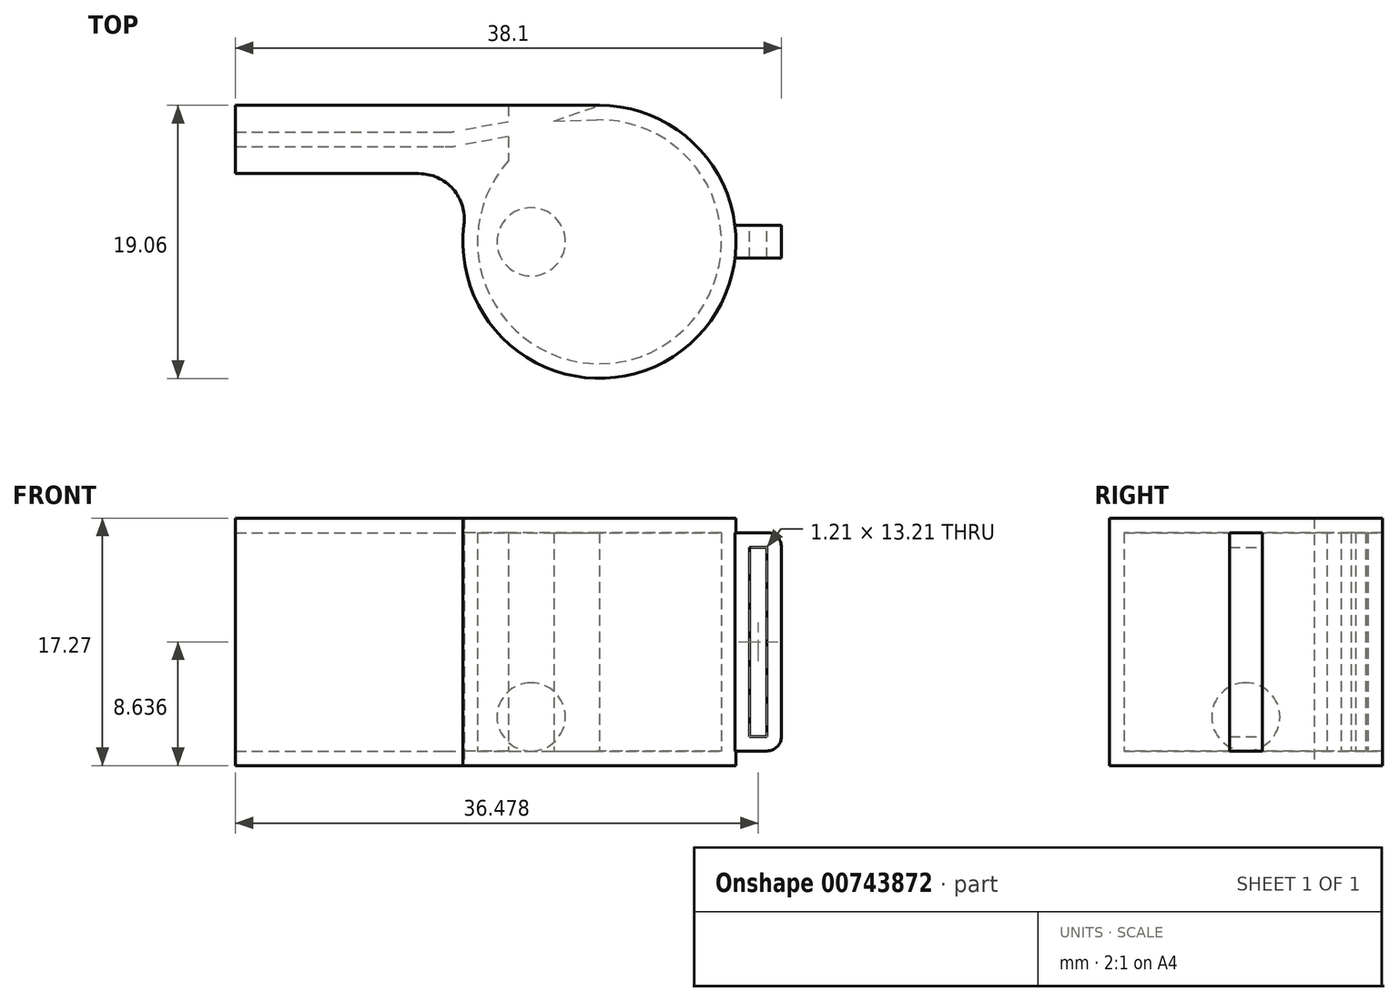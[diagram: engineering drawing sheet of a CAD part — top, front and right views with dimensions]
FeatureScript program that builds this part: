
annotation { "Feature Type Name" : "Feature", "Feature Type Description" : "" }
export const myFeature = defineFeature(function(context is Context, id is Id, definition is map)
    precondition{}
    {
        {
            var Q0;
            Q0=qCreatedBy(makeId("Top.planeOp"),FACE);
            var sketch = newSketch(context, id + "F0", { "sketchPlane" : qUnion([Q0])});
            skArc(sketch, "E0", {"start": v(-9.45, 1.2) * mm, "mid": v(6.3, -7.14) * mm, "end": v(0, 9.53) * mm});
            skLineSegment(sketch, "E1", {"start": v(-6.35, 9.53) * mm, "end": v(-25.4, 9.53) * mm});
            skLineSegment(sketch, "E2", {"start": v(-25.4, 9.52) * mm, "end": v(-25.4, 4.76) * mm});
            skLineSegment(sketch, "E3", {"start": v(-25.4, 4.76) * mm, "end": v(-12.6, 4.76) * mm});
            skPoint(sketch, "E4.visualSharp", {"position": v(-8.25, 4.76) * mm});
            skArc(sketch, "E4.filletArc", {"start": v(-9.45, 1.2) * mm, "mid": v(-10.22, 3.69) * mm, "end": v(-12.6, 4.76) * mm});
            skArc(sketch, "E5.0", {"start": v(-8.44, 1.06) * mm, "mid": v(5.7, -6.32) * mm, "end": v(-0.2, 8.5) * mm, "construction": true});
            skLineSegment(sketch, "E6", {"start": v(-3.18, 7.9) * mm, "end": v(-3.18, 8.98) * mm});
            skPoint(sketch, "E7.orphan", {"position": v(0, 9.53) * mm});
            skLineSegment(sketch, "E8", {"start": v(-3.18, 8.44) * mm, "end": v(0, 9.53) * mm, "construction": true});
            skLineSegment(sketch, "E9", {"start": v(-3.18, 8.44) * mm, "end": v(0, 8.51) * mm, "construction": true});
            skArc(sketch, "E10.trimOffspring", {"start": v(-3.18, 7.9) * mm, "mid": v(-3.56, 7.73) * mm, "end": v(-3.93, 7.55) * mm, "construction": true});
            skArc(sketch, "E11.trimOffspring", {"start": v(-3.17, 8.98) * mm, "mid": v(-3.74, 8.76) * mm, "end": v(-4.28, 8.5) * mm, "construction": true});
            skLineSegment(sketch, "E12", {"start": v(-6.35, 18.63) * mm, "end": v(-6.35, 7.34) * mm});
            skLineSegment(sketch, "E13", {"start": v(0, 9.53) * mm, "end": v(0, 8.51) * mm, "construction": true});
            skLineSegment(sketch, "E14", {"start": v(0, 9.02) * mm, "end": v(-17.36, 5.84) * mm, "construction": true});
            skLineSegment(sketch, "E15", {"start": v(-25.4, 7.14) * mm, "end": v(-7.63, 7.14) * mm, "construction": true});
            skLineSegment(sketch, "E16.0", {"start": v(-0.1, 9.52) * mm, "end": v(-9.73, 7.76) * mm, "construction": true});
            skLineSegment(sketch, "E17.0", {"start": v(0.1, 8.52) * mm, "end": v(-9.63, 6.74) * mm, "construction": true});
            skLineSegment(sketch, "E18.0", {"start": v(-25.4, 6.64) * mm, "end": v(-10.78, 6.64) * mm});
            skLineSegment(sketch, "E19.0", {"start": v(-25.4, 7.65) * mm, "end": v(-10.87, 7.65) * mm});
            skPoint(sketch, "E20.visualSharp", {"position": v(-10.3, 7.65) * mm});
            skArc(sketch, "E20.filletArc", {"start": v(-10.87, 7.65) * mm, "mid": v(-10.3, 7.68) * mm, "end": v(-9.73, 7.76) * mm});
            skPoint(sketch, "E21.visualSharp", {"position": v(-10.2, 6.64) * mm});
            skArc(sketch, "E21.filletArc", {"start": v(-10.78, 6.64) * mm, "mid": v(-10.2, 6.66) * mm, "end": v(-9.63, 6.74) * mm});
            skLineSegment(sketch, "E22", {"start": v(-6.35, 9.53) * mm, "end": v(0, 9.53) * mm});
            skSolve(sketch);
        }
        {
            var Q0;
            Q0=makeQuery(id+"F0.imprint","IMPRINT",FACE,{"disambiguationData":[TD([[makeQuery(id+"F0.imprint","IMPRINT",EDGE,{"derivedFrom":sQuery(id+"F0.wireOp",EDGE,"E0")}),1.0]])]});
            extrude(context, id + "F1", {"entities" : qUnion([Q0]), "depth" : 1.02 * mm, "offsetDistance" : 25.4 * mm});
        }
        {
            var Q0;
            Q0=makeQuery(id+"F1.opExtrude","CAP_FACE",FACE,{"disambiguationData":[OSD([sQuery(id+"F0.wireOp",EDGE,"E0"),sQuery(id+"F0.wireOp",EDGE,"E1"),sQuery(id+"F0.wireOp",EDGE,"E2"),sQuery(id+"F0.wireOp",EDGE,"E3"),sQuery(id+"F0.wireOp",EDGE,"E4.filletArc"),sQuery(id+"F0.wireOp",EDGE,"E22")])],"isStart":false});
            var sketch = newSketch(context, id + "F2", { "sketchPlane" : qUnion([Q0]), "disableImprinting" : false});
            skLineSegment(sketch, "E23.0", {"start": v(-25.4, 7.65) * mm, "end": v(-10.87, 7.65) * mm});
            skLineSegment(sketch, "E24.0", {"start": v(-25.4, 6.64) * mm, "end": v(-10.78, 6.64) * mm});
            skArc(sketch, "E25.0", {"start": v(-10.87, 7.65) * mm, "mid": v(-10.3, 7.68) * mm, "end": v(-9.73, 7.76) * mm});
            skArc(sketch, "E26.0", {"start": v(-10.78, 6.64) * mm, "mid": v(-10.2, 6.66) * mm, "end": v(-9.63, 6.74) * mm});
            skLineSegment(sketch, "E27.0", {"start": v(0.1, 8.52) * mm, "end": v(0.04, 8.5) * mm});
            skLineSegment(sketch, "E28.0", {"start": v(-6.35, 8.37) * mm, "end": v(-9.73, 7.76) * mm});
            skLineSegment(sketch, "E29.0", {"start": v(-3.18, 8.44) * mm, "end": v(0, 8.51) * mm});
            skLineSegment(sketch, "E30.0", {"start": v(-3.18, 8.44) * mm, "end": v(0, 9.53) * mm});
            skArc(sketch, "E31.0", {"start": v(-6.35, 5.66) * mm, "mid": v(3.57, -7.72) * mm, "end": v(-0.2, 8.5) * mm});
            skPoint(sketch, "E32.orphan", {"position": v(-8.44, 1.06) * mm});
            skLineSegment(sketch, "E33.0", {"start": v(-6.35, 9.53) * mm, "end": v(-6.35, 8.37) * mm});
            skPoint(sketch, "E34.orphan", {"position": v(-6.35, 7.34) * mm});
            skLineSegment(sketch, "E35.trimOffspring", {"start": v(-6.35, 7.34) * mm, "end": v(-6.35, 5.66) * mm});
            skLineSegment(sketch, "E36.0", {"start": v(-6.35, 9.53) * mm, "end": v(0, 9.53) * mm, "construction": true});
            skPoint(sketch, "E37.orphan", {"position": v(-6.35, 18.63) * mm});
            skLineSegment(sketch, "E38.0", {"start": v(-6.35, 9.53) * mm, "end": v(-25.4, 9.53) * mm});
            skLineSegment(sketch, "E39.0", {"start": v(-25.4, 9.52) * mm, "end": v(-25.4, 7.65) * mm});
            skLineSegment(sketch, "E40.0", {"start": v(-25.4, 4.76) * mm, "end": v(-12.6, 4.76) * mm});
            skArc(sketch, "E41.0", {"start": v(-9.45, 1.2) * mm, "mid": v(-10.22, 3.69) * mm, "end": v(-12.6, 4.76) * mm});
            skArc(sketch, "E42.0", {"start": v(-9.45, 1.2) * mm, "mid": v(-1.17, -9.45) * mm, "end": v(9.46, -1.14) * mm});
            skLineSegment(sketch, "E43.trimOffspring", {"start": v(-6.35, 7.34) * mm, "end": v(-9.63, 6.74) * mm});
            skPoint(sketch, "E44.orphan", {"position": v(-0.1, 9.52) * mm});
            skLineSegment(sketch, "E45.trimOffspring", {"start": v(-25.4, 6.64) * mm, "end": v(-25.4, 4.76) * mm});
            skLineSegment(sketch, "E46", {"start": v(0, 0) * mm, "end": v(13.97, 0) * mm, "construction": true});
            skLineSegment(sketch, "E47.0", {"start": v(0, -1.14) * mm, "end": v(8.43, -1.14) * mm, "construction": true});
            skLineSegment(sketch, "E48.0", {"start": v(0, 1.14) * mm, "end": v(8.43, 1.14) * mm, "construction": true});
            skLineSegment(sketch, "E49", {"start": v(12.7, 1.14) * mm, "end": v(12.7, -1.14) * mm});
            skLineSegment(sketch, "E50.trimOffspring", {"start": v(9.46, -1.14) * mm, "end": v(12.7, -1.14) * mm});
            skLineSegment(sketch, "E51.trimOffspring", {"start": v(9.46, 1.14) * mm, "end": v(12.7, 1.14) * mm});
            skArc(sketch, "E52.trimOffspring", {"start": v(9.46, 1.14) * mm, "mid": v(6.32, 7.13) * mm, "end": v(0, 9.52) * mm});
            skSolve(sketch);
        }
        {
            var Q0;
            Q0=makeQuery(id+"F2.imprint","IMPRINT",FACE,{"disambiguationData":[TD([[makeQuery(id+"F2.imprint","IMPRINT",EDGE,{"derivedFrom":sQuery(id+"F2.wireOp",EDGE,"E24.0")}),-1.0]])]});
            var Q1;
            Q1=makeQuery(id+"F2.imprint","IMPRINT",FACE,{"disambiguationData":[TD([[makeQuery(id+"F2.imprint","IMPRINT",EDGE,{"derivedFrom":sQuery(id+"F2.wireOp",EDGE,"E23.0")}),1.0]])]});
            var Q2;
            Q2=makeQuery(id+"F2.imprint","IMPRINT",FACE,{"disambiguationData":[TD([[makeQuery(id+"F2.imprint","IMPRINT",EDGE,{"derivedFrom":sQuery(id+"F2.wireOp",EDGE,"E49")}),-1.0]])]});
            extrude(context, id + "F3", {"entities" : qUnion([Q0, Q1, Q2]), "operationType" : NewBodyOperationType.ADD, "depth" : 15.24 * mm, "offsetDistance" : 25.4 * mm});
        }
        {
            var Q0;
            Q0=qCreatedBy(makeId("Front.planeOp"),FACE);
            var sketch = newSketch(context, id + "F4", { "sketchPlane" : qUnion([Q0])});
            skLineSegment(sketch, "E53.0", {"start": v(-9.53, 0) * mm, "end": v(9.53, 0) * mm, "construction": true});
            skLineSegment(sketch, "E54.0", {"start": v(-9.53, 1.02) * mm, "end": v(9.53, 1.02) * mm, "construction": true});
            skArc(sketch, "E55", {"start": v(-4.76, 1.02) * mm, "mid": v(-2.38, 3.4) * mm, "end": v(-4.76, 5.78) * mm});
            skLineSegment(sketch, "E56", {"start": v(-4.76, 0) * mm, "end": v(-4.76, 10.25) * mm, "construction": true});
            skLineSegment(sketch, "E57", {"start": v(-4.76, 5.78) * mm, "end": v(-4.76, 5.27) * mm});
            skLineSegment(sketch, "E58", {"start": v(-4.76, 1.52) * mm, "end": v(-4.76, 1.02) * mm});
            skLineSegment(sketch, "E59", {"start": v(-4.76, 5.27) * mm, "end": v(-4.76, 1.52) * mm});
            skSolve(sketch);
        }
        {
            var Q0;
            Q0 = qSketchRegion(id + "F4", true);
            var Q1;
            Q1=sQuery(id+"F4.wireOp",EDGE,"E56");
            revolve(context, id + "F5", {"surfaceOperationType" : NewSurfaceOperationType.NEW, "entities" : qUnion([Q0]), "axis" : qUnion([Q1]), "revolveType" : RevolveType.FULL});
        }
        {
            var Q0;
            Q0=makeQuery(id+"F3.opExtrude","CAP_FACE",FACE,{"disambiguationData":[OSD([sQuery(id+"F2.wireOp",EDGE,"E24.0"),sQuery(id+"F2.wireOp",EDGE,"E26.0"),sQuery(id+"F2.wireOp",EDGE,"E29.0"),sQuery(id+"F2.wireOp",EDGE,"E30.0"),sQuery(id+"F2.wireOp",EDGE,"E31.0"),sQuery(id+"F2.wireOp",EDGE,"E35.trimOffspring"),sQuery(id+"F2.wireOp",EDGE,"E40.0"),sQuery(id+"F2.wireOp",EDGE,"E41.0"),sQuery(id+"F2.wireOp",EDGE,"E42.0"),sQuery(id+"F2.wireOp",EDGE,"E43.trimOffspring"),sQuery(id+"F2.wireOp",EDGE,"E45.trimOffspring")])],"isStart":false});
            var sketch = newSketch(context, id + "F6", { "sketchPlane" : qUnion([Q0])});
            skLineSegment(sketch, "E60.0", {"start": v(-25.4, 9.52) * mm, "end": v(-25.4, 4.76) * mm});
            skLineSegment(sketch, "E61.0", {"start": v(-6.35, 9.53) * mm, "end": v(-25.4, 9.53) * mm});
            skLineSegment(sketch, "E62.0", {"start": v(-25.4, 4.76) * mm, "end": v(-12.6, 4.76) * mm});
            skArc(sketch, "E63.0", {"start": v(-9.45, 1.2) * mm, "mid": v(-10.22, 3.69) * mm, "end": v(-12.6, 4.76) * mm});
            skArc(sketch, "E64.0", {"start": v(-9.45, 1.2) * mm, "mid": v(6.3, -7.14) * mm, "end": v(0, 9.53) * mm});
            skLineSegment(sketch, "E65.0", {"start": v(-6.35, 9.53) * mm, "end": v(0, 9.53) * mm});
            skSolve(sketch);
        }
        {
            var Q0;
            Q0 = qSketchRegion(id + "F6", true);
            extrude(context, id + "F7", {"entities" : qUnion([Q0]), "operationType" : NewBodyOperationType.ADD, "depth" : 1.02 * mm, "offsetDistance" : 25.4 * mm});
        }
        {
            var Q0;
            Q0=makeQuery(id+"F3.opExtrude","SWEPT_FACE",FACE,{"disambiguationData":[OSD([sQuery(id+"F2.wireOp",EDGE,"E51.trimOffspring")])]});
            var sketch = newSketch(context, id + "F8", { "sketchPlane" : qUnion([Q0])});
            skLineSegment(sketch, "E66.0", {"start": v(-9.46, 1.02) * mm, "end": v(-11.68, 1.02) * mm, "construction": true});
            skLineSegment(sketch, "E67.0", {"start": v(-12.7, 15.24) * mm, "end": v(-12.7, 2.03) * mm, "construction": true});
            skLineSegment(sketch, "E68.0", {"start": v(-9.46, 16.26) * mm, "end": v(-11.68, 16.26) * mm, "construction": true});
            skPoint(sketch, "E69.visualSharp", {"position": v(-12.7, 1.02) * mm});
            skArc(sketch, "E69.filletArc", {"start": v(-12.7, 2.03) * mm, "mid": v(-12.4, 1.31) * mm, "end": v(-11.68, 1.02) * mm});
            skPoint(sketch, "E70.visualSharp", {"position": v(-12.7, 16.26) * mm});
            skArc(sketch, "E70.filletArc", {"start": v(-11.68, 16.26) * mm, "mid": v(-12.4, 15.96) * mm, "end": v(-12.7, 15.24) * mm});
            skLineSegment(sketch, "E71.0", {"start": v(-11.68, 15.24) * mm, "end": v(-11.68, 2.03) * mm});
            skLineSegment(sketch, "E72.0", {"start": v(-10.47, 15.24) * mm, "end": v(-10.47, 2.03) * mm});
            skLineSegment(sketch, "E73.0", {"start": v(-10.47, 2.03) * mm, "end": v(-11.68, 2.03) * mm});
            skLineSegment(sketch, "E74.0", {"start": v(-10.47, 15.24) * mm, "end": v(-11.68, 15.24) * mm});
            skSolve(sketch);
        }
        {
            var Q0;
            {var subQ0=sQuery(id+"F8.wireOp",EDGE,"E69.filletArc");Q0=makeQuery(id+"F8.imprint","IMPRINT",FACE,{"disambiguationData":[TD([[makeQuery(id+"F8.imprint","IMPRINT",EDGE,{"derivedFrom":subQ0}),-1.0]])]});}
            var Q1;
            {var subQ0=sQuery(id+"F8.wireOp",EDGE,"E70.filletArc");Q1=makeQuery(id+"F8.imprint","IMPRINT",FACE,{"disambiguationData":[TD([[makeQuery(id+"F8.imprint","IMPRINT",EDGE,{"derivedFrom":subQ0}),-1.0]])]});}
            var Q2;
            Q2=makeQuery(id+"F8.imprint","IMPRINT",FACE,{"disambiguationData":[TD([[makeQuery(id+"F8.imprint","IMPRINT",EDGE,{"derivedFrom":sQuery(id+"F8.wireOp",EDGE,"E71.0")}),1.0]])]});
            extrude(context, id + "F9", {"entities" : qUnion([Q0, Q1, Q2]), "operationType" : NewBodyOperationType.REMOVE, "oppositeDirection" : true, "depth" : 25.4 * mm, "offsetDistance" : 25.4 * mm});
        }
    });
